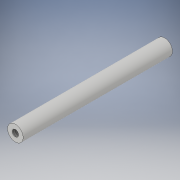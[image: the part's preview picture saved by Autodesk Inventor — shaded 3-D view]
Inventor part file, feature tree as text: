
AUTODESK INVENTOR PART (.ipt)
format: ipt  version: 2017 (Build 210142000, 142)  size: 97,280 bytes
history: native  units: in
note: dims shown in document units (in); Inventor stores cm internally (conversion verified against a paired STEP export)
features: sketch x2, extrude x1, hole x1
ambient origin geometry x8: Origin, YZ Plane, XZ Plane, XY Plane, X Axis, Y Axis, Z Axis, Center Point
bodies: Solid1 (feature_tree)
feature tree (4):
  extrude  "Extrusion1"  Depth=3.346in TaperAngle=0.0deg
  hole  "Hole1"  [1 undecoded]
  sketch  "Sketch1"  dims[d1=0.35in d2=3.346in d3=0.0in]
  sketch  "Sketch2"  dims[d5=0.145in d6=0.38in d7=0.375in d8=0.25in d9=0.5635in d10=0.588in d11=0.8108in]
note: 1 required parameter value undecoded (feature->parameter linkage not recoverable at this tier; creation-order binding heuristic only, values carry confidence <= 0.55)
